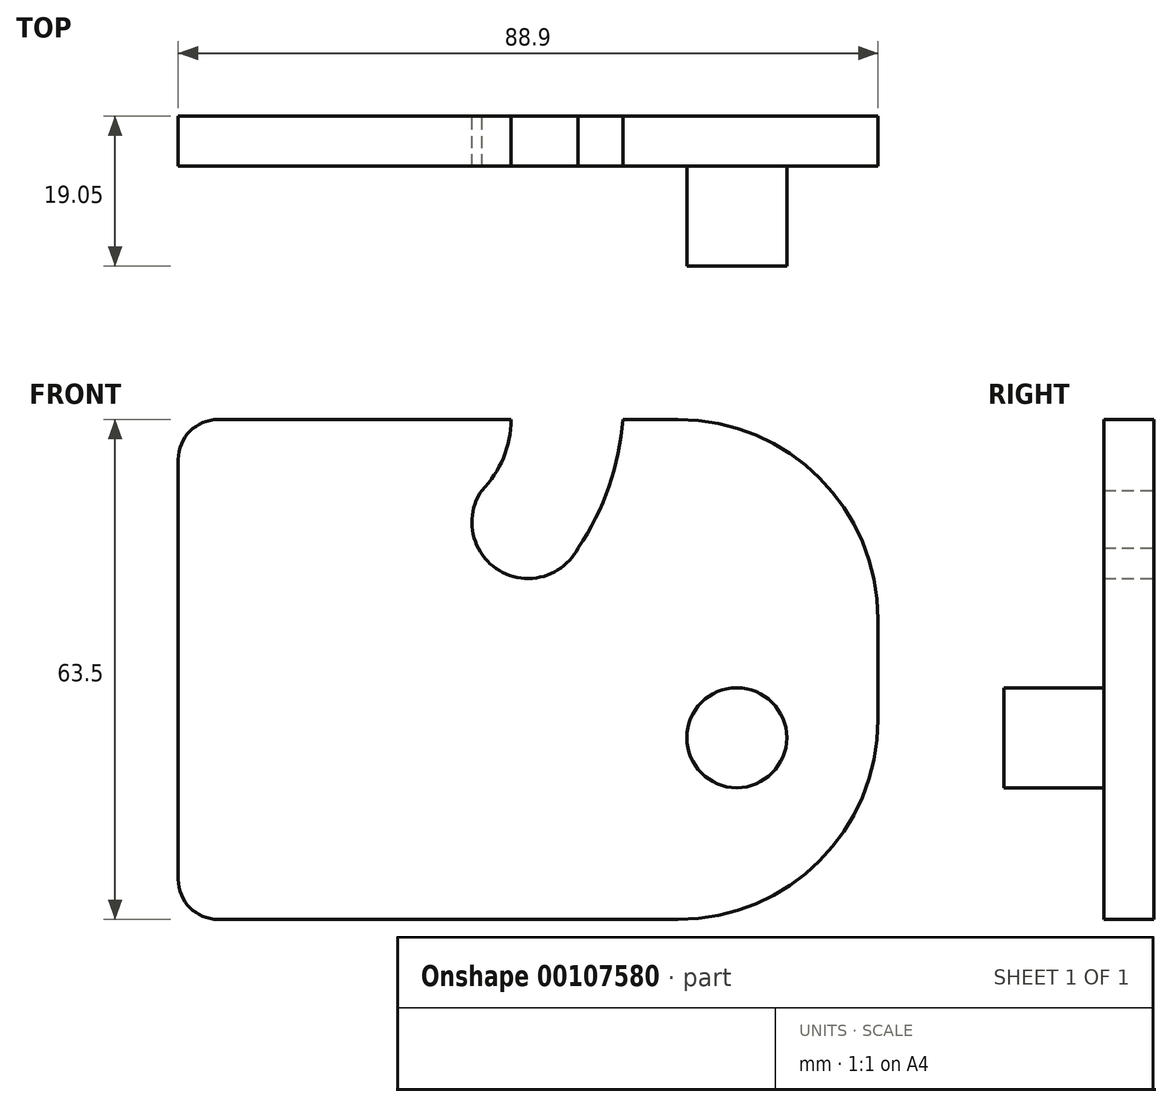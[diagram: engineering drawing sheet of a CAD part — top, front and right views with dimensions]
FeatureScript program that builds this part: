
annotation { "Feature Type Name" : "Feature", "Feature Type Description" : "" }
export const myFeature = defineFeature(function(context is Context, id is Id, definition is map)
    precondition{}
    {
        {
            var Q0;
            Q0=qCreatedBy(makeId("Front.planeOp"),FACE);
            var sketch = newSketch(context, id + "F0", { "sketchPlane" : qUnion([Q0])});
            skLineSegment(sketch, "E0.bottom", {"start": v(44.45, -31.75) * mm, "end": v(-44.45, -31.75) * mm});
            skLineSegment(sketch, "E0.top", {"start": v(44.45, 31.75) * mm, "end": v(-44.45, 31.75) * mm});
            skLineSegment(sketch, "E0.left", {"start": v(44.45, -31.75) * mm, "end": v(44.45, 31.75) * mm});
            skLineSegment(sketch, "E0.right", {"start": v(-44.45, -31.75) * mm, "end": v(-44.45, 31.75) * mm});
            skPoint(sketch, "E0.middle", {"position": v(0, 0) * mm});
            skLineSegment(sketch, "E1", {"start": v(-12.7, 31.75) * mm, "end": v(-12.7, -31.75) * mm, "construction": true});
            skArc(sketch, "E2", {"start": v(6.36, 15.45) * mm, "mid": v(10.26, 23.23) * mm, "end": v(12.02, 31.75) * mm});
            skLineSegment(sketch, "E3", {"start": v(-2.17, 31.75) * mm, "end": v(-2.17, -31.75) * mm, "construction": true});
            skArc(sketch, "E4", {"start": v(-5.89, 22.75) * mm, "mid": v(-3.14, 26.88) * mm, "end": v(-2.17, 31.75) * mm});
            skArc(sketch, "E5.trimOffspring", {"start": v(-5.89, 22.75) * mm, "mid": v(-3.66, 12.57) * mm, "end": v(6.36, 15.45) * mm});
            skCircle(sketch, "E6", {"center": v(0, 18.7) * mm, "radius": 38.1 * mm, "construction": true});
            skCircle(sketch, "E7", {"center": v(26.5, -8.67) * mm, "radius": 6.35 * mm});
            skSolve(sketch);
        }
        {
            var Q0;
            Q0=makeQuery(id+"F0.imprint","IMPRINT",FACE,{"disambiguationData":[TD([[makeQuery(id+"F0.imprint","IMPRINT",EDGE,{"derivedFrom":sQuery(id+"F0.wireOp",EDGE,"E0.bottom")}),-1.0]])]});
            var Q1;
            Q1=makeQuery(id+"F0.imprint","IMPRINT",FACE,{"disambiguationData":[TD([[makeQuery(id+"F0.imprint","IMPRINT",EDGE,{"derivedFrom":sQuery(id+"F0.wireOp",EDGE,"E7")}),1.0]])]});
            extrude(context, id + "F1", {"entities" : qUnion([Q0, Q1]), "depth" : 6.35 * mm});
        }
        {
            var Q0;
            Q0=makeQuery(id+"F1.opExtrude","SWEPT_EDGE",EDGE,{"disambiguationData":[OSD([sQuery(id+"F0.wireOp",EDGE,"E0.bottom"),sQuery(id+"F0.wireOp",EDGE,"E0.left")])]});
            var Q1;
            Q1=makeQuery(id+"F1.opExtrude","SWEPT_EDGE",EDGE,{"disambiguationData":[OSD([sQuery(id+"F0.wireOp",EDGE,"E0.top"),sQuery(id+"F0.wireOp",EDGE,"E0.left")])]});
            fillet(context, id + "F2", {"entities" : qUnion([Q0, Q1]), "radius" : 25.4 * mm, "tangentPropagation" : true, "allowEdgeOverflow" : false});
        }
        {
            var Q0;
            Q0=makeQuery(id+"F1.opExtrude","SWEPT_EDGE",EDGE,{"disambiguationData":[OSD([sQuery(id+"F0.wireOp",EDGE,"E0.top"),sQuery(id+"F0.wireOp",EDGE,"E0.right")])]});
            var Q1;
            Q1=makeQuery(id+"F1.opExtrude","SWEPT_EDGE",EDGE,{"disambiguationData":[OSD([sQuery(id+"F0.wireOp",EDGE,"E0.bottom"),sQuery(id+"F0.wireOp",EDGE,"E0.right")])]});
            fillet(context, id + "F3", {"entities" : qUnion([Q0, Q1]), "radius" : 5.08 * mm, "tangentPropagation" : true, "allowEdgeOverflow" : false});
        }
        {
            var Q0;
            Q0=makeQuery(id+"F0.imprint","IMPRINT",FACE,{"disambiguationData":[TD([[makeQuery(id+"F0.imprint","IMPRINT",EDGE,{"derivedFrom":sQuery(id+"F0.wireOp",EDGE,"E7")}),1.0]])]});
            extrude(context, id + "F4", {"entities" : qUnion([Q0]), "operationType" : NewBodyOperationType.ADD, "depth" : 19.05 * mm});
        }
    });
